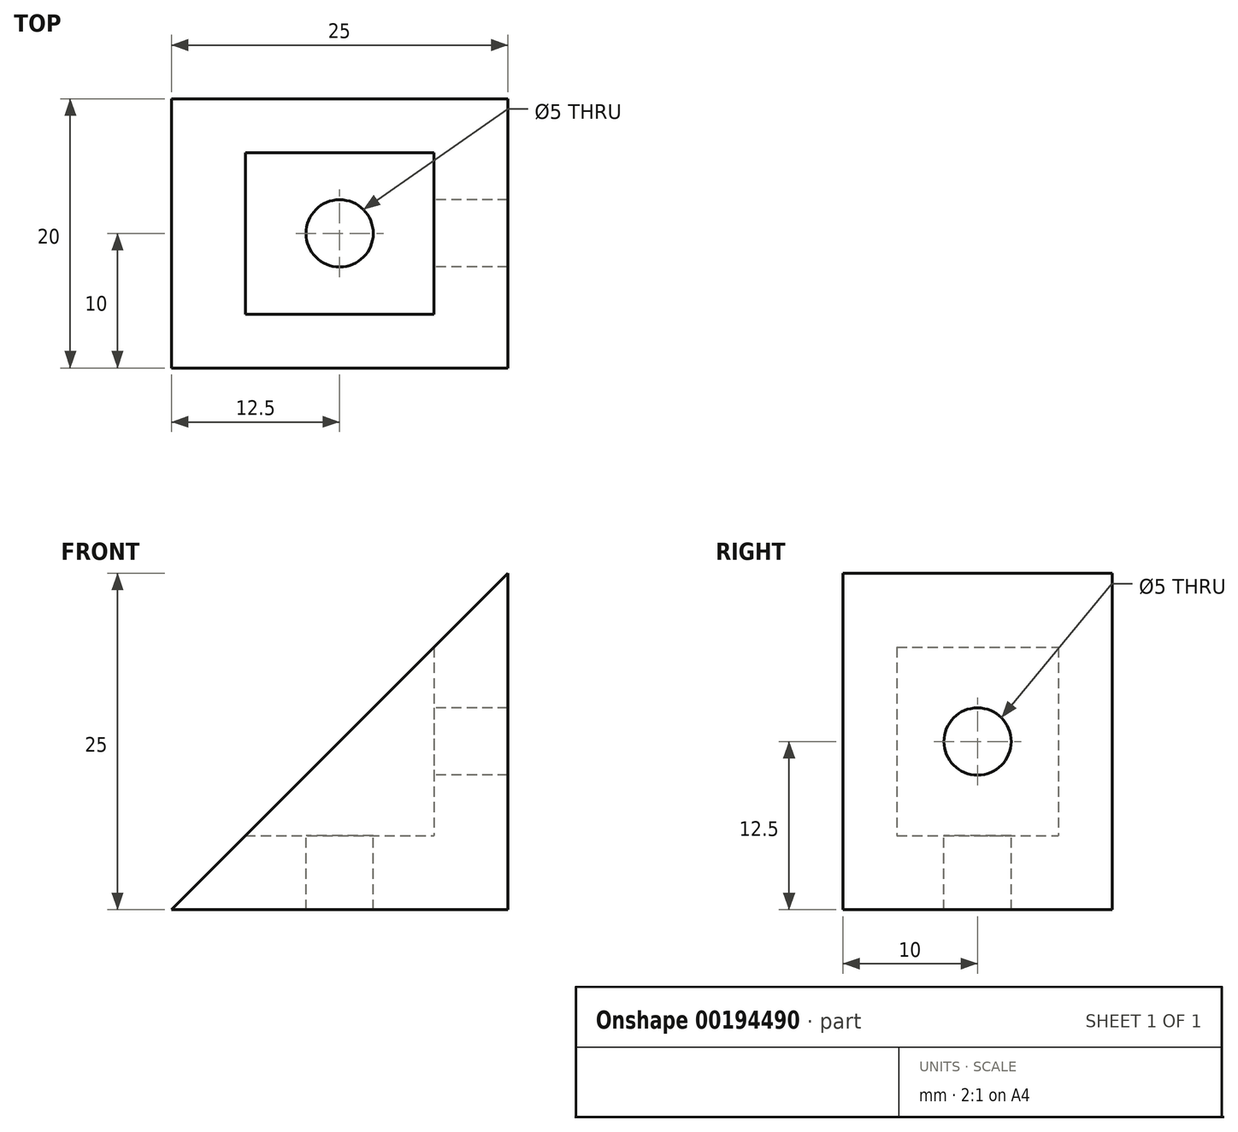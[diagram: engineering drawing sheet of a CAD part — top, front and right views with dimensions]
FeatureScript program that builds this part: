
annotation { "Feature Type Name" : "Feature", "Feature Type Description" : "" }
export const myFeature = defineFeature(function(context is Context, id is Id, definition is map)
    precondition{}
    {
        {
            var Q0;
            Q0=qCreatedBy(makeId("Front.planeOp"),FACE);
            var sketch = newSketch(context, id + "F0", { "sketchPlane" : qUnion([Q0])});
            skLineSegment(sketch, "E0.top", {"start": v(-12.5, -12.5) * mm, "end": v(12.5, -12.5) * mm});
            skLineSegment(sketch, "E0.right", {"start": v(12.5, 12.5) * mm, "end": v(12.5, -12.5) * mm});
            skPoint(sketch, "E0.middle", {"position": v(0, 0) * mm});
            skLineSegment(sketch, "E1", {"start": v(12.5, -12.5) * mm, "end": v(12.5, -7) * mm});
            skLineSegment(sketch, "E2", {"start": v(12.5, -7) * mm, "end": v(12.5, -12.5) * mm});
            skLineSegment(sketch, "E3", {"start": v(12.5, -12.5) * mm, "end": v(7, -12.5) * mm});
            skLineSegment(sketch, "E4", {"start": v(-7, -7) * mm, "end": v(-12.5, -12.5) * mm});
            skLineSegment(sketch, "E5", {"start": v(12.5, -12.5) * mm, "end": v(12.5, 12.5) * mm});
            skLineSegment(sketch, "E6", {"start": v(12.5, 12.5) * mm, "end": v(7, 7) * mm});
            skLineSegment(sketch, "E7", {"start": v(7, 7) * mm, "end": v(7, -7) * mm});
            skLineSegment(sketch, "E8", {"start": v(-7, -7) * mm, "end": v(7, -7) * mm});
            skLineSegment(sketch, "E9", {"start": v(-7, -7) * mm, "end": v(7, 7) * mm});
            skSolve(sketch);
        }
        {
            var Q0;
            Q0=makeQuery(id+"F0.imprint","IMPRINT",FACE,{"disambiguationData":[TD([[makeQuery(id+"F0.imprint","IMPRINT",EDGE,{"derivedFrom":sQuery(id+"F0.wireOp",EDGE,"E0.top")}),1.0]])]});
            extrude(context, id + "F1", {"entities" : qUnion([Q0]), "depth" : 20 * mm});
        }
        {
            var Q0;
            Q0 = qSketchRegion(id + "F0", true);
            extrude(context, id + "F2", {"entities" : qUnion([Q0]), "operationType" : NewBodyOperationType.ADD, "depth" : 4 * mm});
        }
        {
            var Q0;
            Q0=makeQuery(id+"F1.opExtrude","CAP_FACE",FACE,{"disambiguationData":[OSD([sQuery(id+"F0.wireOp",EDGE,"E0.top"),sQuery(id+"F0.wireOp",EDGE,"E3"),sQuery(id+"F0.wireOp",EDGE,"E4"),sQuery(id+"F0.wireOp",EDGE,"E5"),sQuery(id+"F0.wireOp",EDGE,"E6"),sQuery(id+"F0.wireOp",EDGE,"E7"),sQuery(id+"F0.wireOp",EDGE,"E8")])],"isStart":false});
            var sketch = newSketch(context, id + "F3", { "sketchPlane" : qUnion([Q0])});
            skLineSegment(sketch, "E10", {"start": v(-12.5, -12.5) * mm, "end": v(12.5, -12.5) * mm});
            skLineSegment(sketch, "E11", {"start": v(12.5, -12.5) * mm, "end": v(12.5, 12.5) * mm});
            skLineSegment(sketch, "E12", {"start": v(12.5, 12.5) * mm, "end": v(-12.5, -12.5) * mm});
            skSolve(sketch);
        }
        {
            var Q0;
            Q0 = qSketchRegion(id + "F3", true);
            extrude(context, id + "F4", {"entities" : qUnion([Q0]), "operationType" : NewBodyOperationType.ADD, "oppositeDirection" : true, "depth" : 4 * mm});
        }
        {
            var Q0;
            Q0=makeQuery(id+"F1.opExtrude","SWEPT_FACE",FACE,{"disambiguationData":[OSD([sQuery(id+"F0.wireOp",EDGE,"E7")])]});
            var sketch = newSketch(context, id + "F5", { "sketchPlane" : qUnion([Q0])});
            skLineSegment(sketch, "E13", {"start": v(10, -7) * mm, "end": v(10, -2.5) * mm});
            skLineSegment(sketch, "E14", {"start": v(10, 7) * mm, "end": v(10, 2.5) * mm});
            skLineSegment(sketch, "E15", {"start": v(10, 2.5) * mm, "end": v(10, -2.5) * mm});
            skCircle(sketch, "E16", {"center": v(10, 0) * mm, "radius": 2.5 * mm});
            skSolve(sketch);
        }
        {
            var Q0;
            {var subQ0=sQuery(id+"F5.wireOp",EDGE,"E15");Q0=makeQuery(id+"F5.imprint","IMPRINT",FACE,{"disambiguationData":[TD([[makeQuery(id+"F5.imprint","IMPRINT",EDGE,{"derivedFrom":subQ0}),1.0]])]});}
            var Q1;
            {var subQ0=sQuery(id+"F5.wireOp",EDGE,"E15");Q1=makeQuery(id+"F5.imprint","IMPRINT",FACE,{"disambiguationData":[TD([[makeQuery(id+"F5.imprint","IMPRINT",EDGE,{"derivedFrom":subQ0}),-1.0]])]});}
            extrude(context, id + "F6", {"entities" : qUnion([Q0, Q1]), "operationType" : NewBodyOperationType.REMOVE, "oppositeDirection" : true, "depth" : 25.4 * mm});
        }
        {
            var Q0;
            Q0=makeQuery(id+"F1.opExtrude","SWEPT_FACE",FACE,{"disambiguationData":[OSD([sQuery(id+"F0.wireOp",EDGE,"E8")])]});
            var sketch = newSketch(context, id + "F7", { "sketchPlane" : qUnion([Q0])});
            skCircle(sketch, "E17", {"center": v(0, -10) * mm, "radius": 2.5 * mm});
            skSolve(sketch);
        }
        {
            var Q0;
            Q0=makeQuery(id+"F7.imprint","IMPRINT",FACE,{"disambiguationData":[TD([[makeQuery(id+"F7.imprint","IMPRINT",EDGE,{"derivedFrom":sQuery(id+"F7.wireOp",EDGE,"E17")}),1.0]])]});
            extrude(context, id + "F8", {"entities" : qUnion([Q0]), "operationType" : NewBodyOperationType.REMOVE, "oppositeDirection" : true, "depth" : 25.4 * mm});
        }
    });
